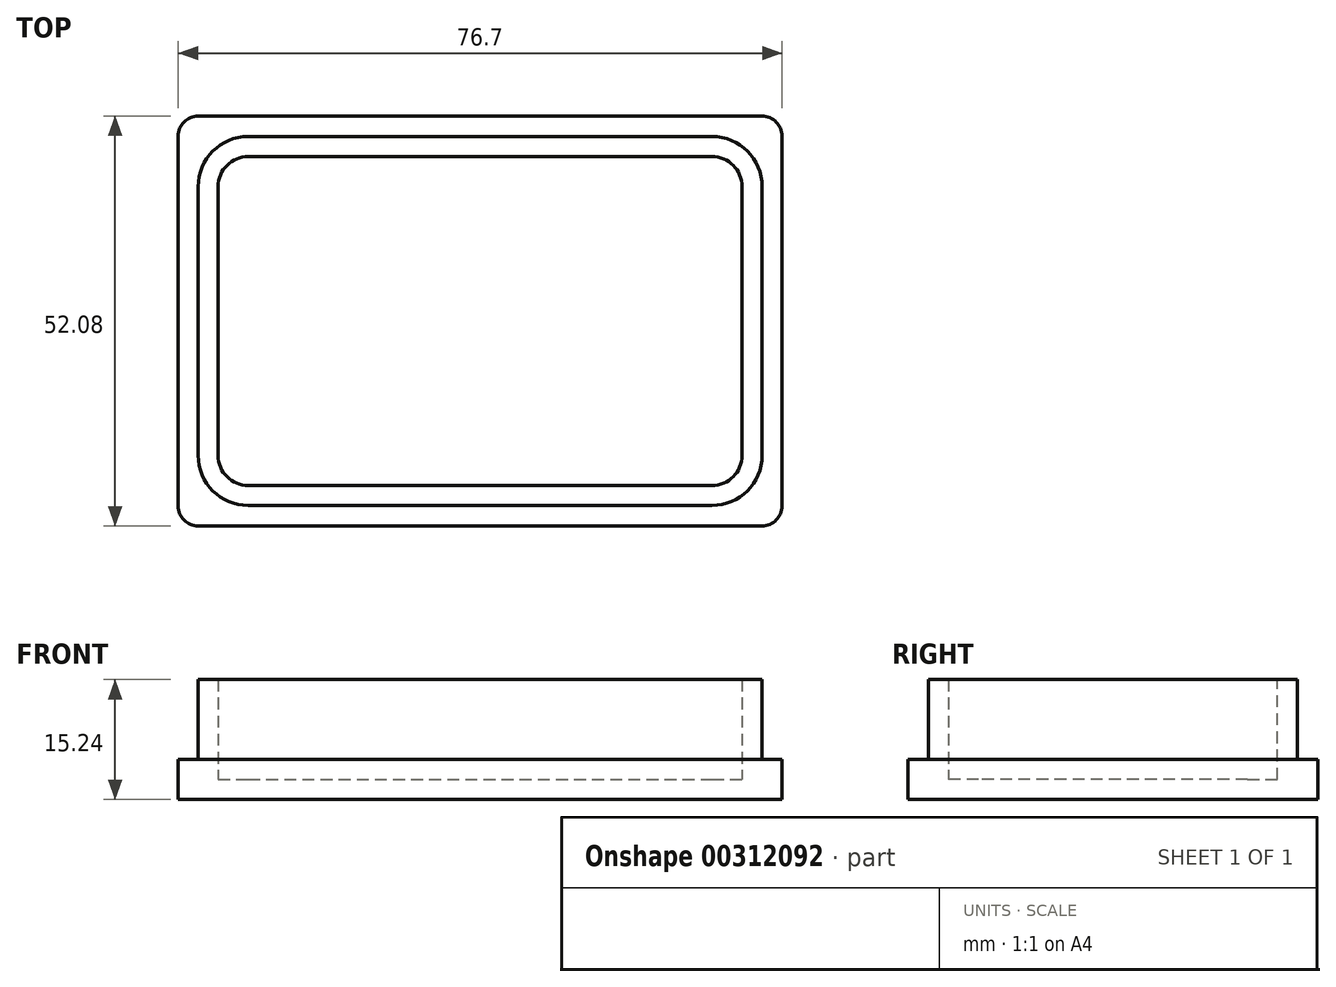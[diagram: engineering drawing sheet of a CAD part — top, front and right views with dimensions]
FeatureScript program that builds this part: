
annotation { "Feature Type Name" : "Feature", "Feature Type Description" : "" }
export const myFeature = defineFeature(function(context is Context, id is Id, definition is map)
    precondition{}
    {
        {
            var Q0;
            Q0=qCreatedBy(makeId("Top.planeOp"),FACE);
            var sketch = newSketch(context, id + "F0", { "sketchPlane" : qUnion([Q0])});
            skLineSegment(sketch, "E0.bottom", {"start": v(-35.81, 26.04) * mm, "end": v(35.81, 26.03) * mm});
            skLineSegment(sketch, "E0.top", {"start": v(-35.81, -26.03) * mm, "end": v(35.81, -26.04) * mm});
            skLineSegment(sketch, "E0.left", {"start": v(-38.35, 23.5) * mm, "end": v(-38.35, -23.5) * mm});
            skLineSegment(sketch, "E0.right", {"start": v(38.35, 23.5) * mm, "end": v(38.35, -23.5) * mm});
            skLineSegment(sketch, "E1.bottom", {"start": v(-29.46, 23.43) * mm, "end": v(29.46, 23.43) * mm});
            skLineSegment(sketch, "E1.top", {"start": v(-29.46, -23.43) * mm, "end": v(29.46, -23.43) * mm});
            skLineSegment(sketch, "E1.left", {"start": v(-35.81, 17.08) * mm, "end": v(-35.81, -17.08) * mm});
            skLineSegment(sketch, "E1.right", {"start": v(35.81, 17.08) * mm, "end": v(35.81, -17.08) * mm});
            skLineSegment(sketch, "E2", {"start": v(0, 52.7) * mm, "end": v(0, -51.02) * mm, "construction": true});
            skLineSegment(sketch, "E3", {"start": v(-51.65, 0) * mm, "end": v(67.19, 0) * mm, "construction": true});
            skPoint(sketch, "E4", {"position": v(-38.35, 0) * mm});
            skPoint(sketch, "E5", {"position": v(-35.81, 0) * mm});
            skPoint(sketch, "E6", {"position": v(0, -26.03) * mm});
            skPoint(sketch, "E7", {"position": v(0, -23.43) * mm});
            skPoint(sketch, "E8.visualSharp", {"position": v(-35.81, 23.43) * mm});
            skArc(sketch, "E8.filletArc", {"start": v(-29.46, 23.43) * mm, "mid": v(-33.95, 21.57) * mm, "end": v(-35.81, 17.08) * mm});
            skPoint(sketch, "E9.visualSharp", {"position": v(-35.81, -23.43) * mm});
            skArc(sketch, "E9.filletArc", {"start": v(-35.81, -17.08) * mm, "mid": v(-33.95, -21.57) * mm, "end": v(-29.46, -23.43) * mm});
            skPoint(sketch, "E10.visualSharp", {"position": v(35.81, 23.43) * mm});
            skArc(sketch, "E10.filletArc", {"start": v(35.81, 17.08) * mm, "mid": v(33.95, 21.57) * mm, "end": v(29.46, 23.43) * mm});
            skPoint(sketch, "E11.visualSharp", {"position": v(35.81, -23.43) * mm});
            skArc(sketch, "E11.filletArc", {"start": v(29.46, -23.43) * mm, "mid": v(33.95, -21.57) * mm, "end": v(35.81, -17.08) * mm});
            skPoint(sketch, "E12.visualSharp", {"position": v(-38.35, 26.04) * mm});
            skArc(sketch, "E12.filletArc", {"start": v(-35.81, 26.03) * mm, "mid": v(-37.61, 25.3) * mm, "end": v(-38.35, 23.5) * mm});
            skPoint(sketch, "E13.visualSharp", {"position": v(38.35, 26.03) * mm});
            skArc(sketch, "E13.filletArc", {"start": v(38.35, 23.5) * mm, "mid": v(37.61, 25.3) * mm, "end": v(35.81, 26.03) * mm});
            skPoint(sketch, "E14.visualSharp", {"position": v(38.35, -26.04) * mm});
            skArc(sketch, "E14.filletArc", {"start": v(35.81, -26.04) * mm, "mid": v(37.61, -25.3) * mm, "end": v(38.35, -23.5) * mm});
            skPoint(sketch, "E15.visualSharp", {"position": v(-38.35, -26.03) * mm});
            skArc(sketch, "E15.filletArc", {"start": v(-38.35, -23.5) * mm, "mid": v(-37.61, -25.3) * mm, "end": v(-35.81, -26.04) * mm});
            skSolve(sketch);
        }
        {
            var Q0;
            Q0=makeQuery(id+"F0.imprint","IMPRINT",FACE,{"disambiguationData":[TD([[makeQuery(id+"F0.imprint","IMPRINT",EDGE,{"derivedFrom":sQuery(id+"F0.wireOp",EDGE,"E0.bottom")}),-1.0]])]});
            extrude(context, id + "F1", {"entities" : qUnion([Q0]), "depth" : 5.08 * mm});
        }
        {
            var Q0;
            Q0=sQuery(id+"F0.wireOp",EDGE,"E1.left");
            var Q1;
            Q1=sQuery(id+"F0.wireOp",EDGE,"E1.bottom");
            var Q2;
            Q2=sQuery(id+"F0.wireOp",EDGE,"E1.right");
            var Q3;
            Q3=sQuery(id+"F0.wireOp",EDGE,"E1.top");
            extrude(context, id + "F2", {"bodyType" : ToolBodyType.SURFACE, "operationType" : NewBodyOperationType.ADD, "surfaceEntities" : qUnion([Q0, Q1, Q2, Q3]), "depth" : 15.24 * mm});
        }
        {
            var Q0;
            Q0=makeQuery(id+"F0.imprint","IMPRINT",FACE,{"disambiguationData":[TD([[makeQuery(id+"F0.imprint","IMPRINT",EDGE,{"derivedFrom":sQuery(id+"F0.wireOp",EDGE,"E1.bottom")}),-1.0]])]});
            extrude(context, id + "F3", {"entities" : qUnion([Q0]), "operationType" : NewBodyOperationType.ADD, "depth" : 15.24 * mm});
        }
        {
            var Q0;
            Q0=makeQuery(id+"F3.opExtrude","CAP_FACE",FACE,{"disambiguationData":[OSD([sQuery(id+"F0.wireOp",EDGE,"E1.bottom"),sQuery(id+"F0.wireOp",EDGE,"E1.top"),sQuery(id+"F0.wireOp",EDGE,"E1.left"),sQuery(id+"F0.wireOp",EDGE,"E1.right")])],"isStart":false});
            shell(context, id + "F4", {"entities" : qUnion([Q0]), "thickness" : 2.54 * mm});
        }
    });
